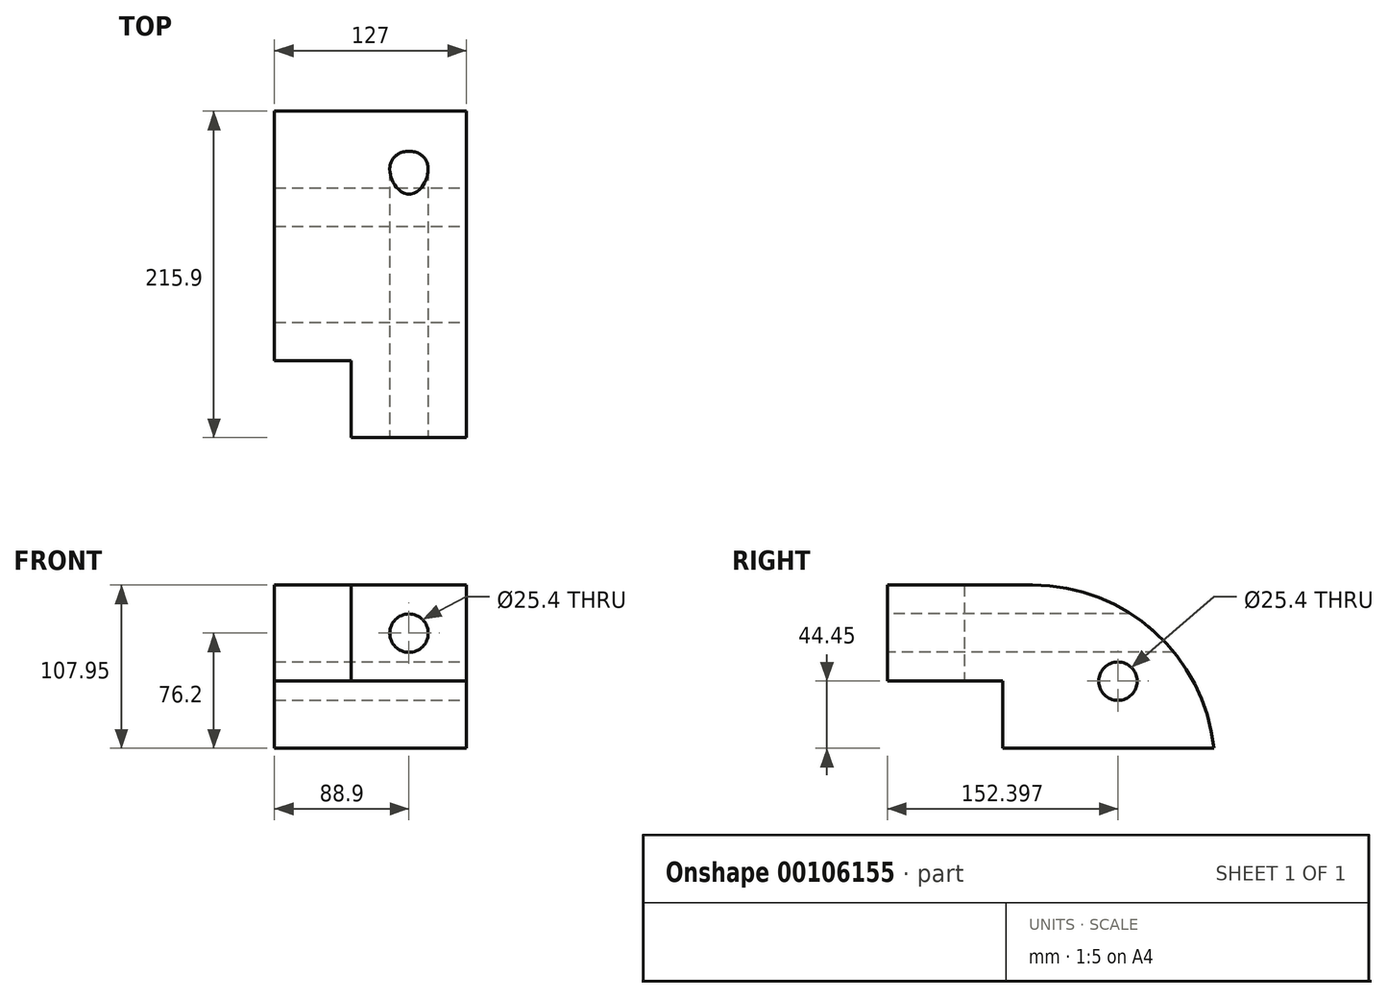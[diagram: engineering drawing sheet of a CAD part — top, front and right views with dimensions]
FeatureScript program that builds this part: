
annotation { "Feature Type Name" : "Feature", "Feature Type Description" : "" }
export const myFeature = defineFeature(function(context is Context, id is Id, definition is map)
    precondition{}
    {
        {
            var Q0;
            Q0=qCreatedBy(makeId("Top.planeOp"),FACE);
            var sketch = newSketch(context, id + "F0", { "sketchPlane" : qUnion([Q0])});
            skLineSegment(sketch, "E0.bottom", {"start": v(0, 74.27) * mm, "end": v(-127, 74.27) * mm});
            skLineSegment(sketch, "E0.top", {"start": v(0, -65.43) * mm, "end": v(-127, -65.43) * mm});
            skLineSegment(sketch, "E0.left", {"start": v(0, 74.27) * mm, "end": v(0, -65.43) * mm});
            skLineSegment(sketch, "E0.right", {"start": v(-127, 74.27) * mm, "end": v(-127, -65.43) * mm});
            skSolve(sketch);
        }
        {
            var Q0;
            Q0=makeQuery(id+"F0.imprint","IMPRINT",FACE,{"disambiguationData":[TD([[makeQuery(id+"F0.imprint","IMPRINT",EDGE,{"derivedFrom":sQuery(id+"F0.wireOp",EDGE,"E0.bottom")}),1.0]])]});
            extrude(context, id + "F1", {"entities" : qUnion([Q0]), "depth" : 107.95 * mm});
        }
        {
            var Q0;
            Q0=makeQuery(id+"F1.opExtrude","CAP_EDGE",EDGE,{"disambiguationData":[OSD([sQuery(id+"F0.wireOp",EDGE,"E0.bottom")])],"isStart":false});
            fillet(context, id + "F2", {"entities" : qUnion([Q0]), "radius" : 120.65 * mm, "tangentPropagation" : true, "allowEdgeOverflow" : false});
        }
        {
            var Q0;
            Q0=makeQuery(id+"F1.opExtrude","SWEPT_FACE",FACE,{"disambiguationData":[OSD([sQuery(id+"F0.wireOp",EDGE,"E0.top")])]});
            var sketch = newSketch(context, id + "F3", { "sketchPlane" : qUnion([Q0])});
            skLineSegment(sketch, "E1.bottom", {"start": v(-127, 107.95) * mm, "end": v(0, 107.95) * mm});
            skLineSegment(sketch, "E1.top", {"start": v(-127, 44.45) * mm, "end": v(0, 44.45) * mm});
            skLineSegment(sketch, "E1.left", {"start": v(-127, 107.95) * mm, "end": v(-127, 44.45) * mm});
            skLineSegment(sketch, "E1.right", {"start": v(0, 107.95) * mm, "end": v(0, 44.45) * mm});
            skSolve(sketch);
        }
        {
            var Q0;
            Q0=makeQuery(id+"F3.imprint","IMPRINT",FACE,{"disambiguationData":[TD([[makeQuery(id+"F3.imprint","IMPRINT",EDGE,{"derivedFrom":sQuery(id+"F3.wireOp",EDGE,"E1.bottom")}),1.0]])]});
            extrude(context, id + "F4", {"entities" : qUnion([Q0]), "operationType" : NewBodyOperationType.ADD, "depth" : 25.4 * mm});
        }
        {
            var Q0;
            Q0=makeQuery(id+"F4.opExtrude","CAP_FACE",FACE,{"disambiguationData":[OSD([sQuery(id+"F3.wireOp",EDGE,"E1.bottom"),sQuery(id+"F3.wireOp",EDGE,"E1.top"),sQuery(id+"F3.wireOp",EDGE,"E1.left"),sQuery(id+"F3.wireOp",EDGE,"E1.right")])],"isStart":false});
            var sketch = newSketch(context, id + "F5", { "sketchPlane" : qUnion([Q0])});
            skLineSegment(sketch, "E2.bottom", {"start": v(0, 107.95) * mm, "end": v(-76.2, 107.95) * mm});
            skLineSegment(sketch, "E2.top", {"start": v(0, 44.45) * mm, "end": v(-76.2, 44.45) * mm});
            skLineSegment(sketch, "E2.left", {"start": v(0, 107.95) * mm, "end": v(0, 44.45) * mm});
            skLineSegment(sketch, "E2.right", {"start": v(-76.2, 107.95) * mm, "end": v(-76.2, 44.45) * mm});
            skSolve(sketch);
        }
        {
            var Q0;
            Q0=makeQuery(id+"F5.imprint","IMPRINT",FACE,{"disambiguationData":[TD([[makeQuery(id+"F5.imprint","IMPRINT",EDGE,{"derivedFrom":sQuery(id+"F5.wireOp",EDGE,"E2.bottom")}),1.0]])]});
            extrude(context, id + "F6", {"entities" : qUnion([Q0]), "operationType" : NewBodyOperationType.ADD, "depth" : 50.8 * mm});
        }
        {
            var Q0;
            Q0=makeQuery(id+"F6.opExtrude","CAP_FACE",FACE,{"disambiguationData":[OSD([sQuery(id+"F5.wireOp",EDGE,"E2.bottom"),sQuery(id+"F5.wireOp",EDGE,"E2.top"),sQuery(id+"F5.wireOp",EDGE,"E2.left"),sQuery(id+"F5.wireOp",EDGE,"E2.right")])],"isStart":false});
            var sketch = newSketch(context, id + "F7", { "sketchPlane" : qUnion([Q0])});
            skLineSegment(sketch, "E3.bottom", {"start": v(0, 107.95) * mm, "end": v(-38.1, 107.95) * mm});
            skLineSegment(sketch, "E3.top", {"start": v(0, 76.2) * mm, "end": v(-38.1, 76.2) * mm});
            skLineSegment(sketch, "E3.left", {"start": v(0, 107.95) * mm, "end": v(0, 76.2) * mm});
            skLineSegment(sketch, "E3.right", {"start": v(-38.1, 107.95) * mm, "end": v(-38.1, 76.2) * mm});
            skSolve(sketch);
        }
        {
            var Q0;
            Q0=sQuery(id+"F7.wireOp",VERTEX,"E3.right.end");
            var Q1;
            Q1=makeQuery(id+"F1.opExtrude","SWEPT_BODY",BODY,{"disambiguationData":[OSD([sQuery(id+"F0.wireOp",EDGE,"E0.bottom"),sQuery(id+"F0.wireOp",EDGE,"E0.top"),sQuery(id+"F0.wireOp",EDGE,"E0.left"),sQuery(id+"F0.wireOp",EDGE,"E0.right")])]});
            hole(context, id + "F8", {"style" : HoleStyle.SIMPLE, "endStyle" : HoleEndStyle.THROUGH, "holeDiameter" : 25.4 * mm, "locations" : qUnion([Q0]), "scope" : qUnion([Q1]), "isTappedThrough" : true});
        }
        {
            var Q0;
            Q0=makeQuery(id+"F6.boolean.opBoolean","MERGE",FACE,{"derivedFrom":[makeQuery(id+"F4.boolean.opBoolean","MERGE",FACE,{"derivedFrom":[makeQuery(id+"F1.opExtrude","SWEPT_FACE",FACE,{"disambiguationData":[OSD([sQuery(id+"F0.wireOp",EDGE,"E0.left")])]}),makeQuery(id+"F4.opExtrude","SWEPT_FACE",FACE,{"disambiguationData":[OSD([sQuery(id+"F3.wireOp",EDGE,"E1.right")])]})]}),makeQuery(id+"F6.opExtrude","SWEPT_FACE",FACE,{"disambiguationData":[OSD([sQuery(id+"F5.wireOp",EDGE,"E2.left")])]})]});
            var sketch = newSketch(context, id + "F9", { "sketchPlane" : qUnion([Q0])});
            skLineSegment(sketch, "E4.bottom", {"start": v(74.27, 0) * mm, "end": v(10.77, 0) * mm});
            skLineSegment(sketch, "E4.top", {"start": v(74.27, 44.45) * mm, "end": v(10.77, 44.45) * mm});
            skLineSegment(sketch, "E4.left", {"start": v(74.27, 0) * mm, "end": v(74.27, 44.45) * mm});
            skLineSegment(sketch, "E4.right", {"start": v(10.77, 0) * mm, "end": v(10.77, 44.45) * mm});
            skSolve(sketch);
        }
        {
            var Q0;
            Q0=sQuery(id+"F9.wireOp",VERTEX,"E4.right.end");
            var Q1;
            Q1=makeQuery(id+"F1.opExtrude","SWEPT_BODY",BODY,{"disambiguationData":[OSD([sQuery(id+"F0.wireOp",EDGE,"E0.bottom"),sQuery(id+"F0.wireOp",EDGE,"E0.top"),sQuery(id+"F0.wireOp",EDGE,"E0.left"),sQuery(id+"F0.wireOp",EDGE,"E0.right")])]});
            hole(context, id + "F10", {"style" : HoleStyle.SIMPLE, "endStyle" : HoleEndStyle.THROUGH, "holeDiameter" : 25.4 * mm, "locations" : qUnion([Q0]), "scope" : qUnion([Q1]), "isTappedThrough" : true});
        }
    });
